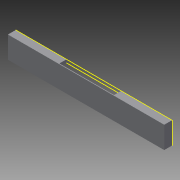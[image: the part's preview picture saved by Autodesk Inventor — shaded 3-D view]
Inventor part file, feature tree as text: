
AUTODESK INVENTOR PART (.ipt)
format: ipt  version: 2013 (Build 170138000, 138)  size: 138,752 bytes
history: native  units: mm
features: sketch x8, extrude x7, other x1
ambient origin geometry x8: Origin, YZ Plane, XZ Plane, XY Plane, X Axis, Y Axis, Z Axis, Center Point
feature tree (16):
  other  "ソリッド1"
  extrude  "押し出し1"  Depth=90.0mm
  extrude  "押し出し2"  Depth=10.0mm
  extrude  "押し出し3"  Depth=0.5mm TaperAngle=0.0deg
  extrude  "押し出し4"  Depth=5.0mm
  extrude  "押し出し5"  Depth=5.0mm TaperAngle=0.0deg
  extrude  "押し出し6"  Depth=5.0mm TaperAngle=0.0deg
  sketch  "スケッチ7"
  extrude  "押し出し7"  Depth=5.0mm TaperAngle=0.0deg
  sketch  "スケッチ1"
  sketch  "スケッチ2"
  sketch  "スケッチ3"
  sketch  "スケッチ4"
  sketch  "スケッチ5"
  sketch  "スケッチ6"
  sketch  "スケッチ8"
